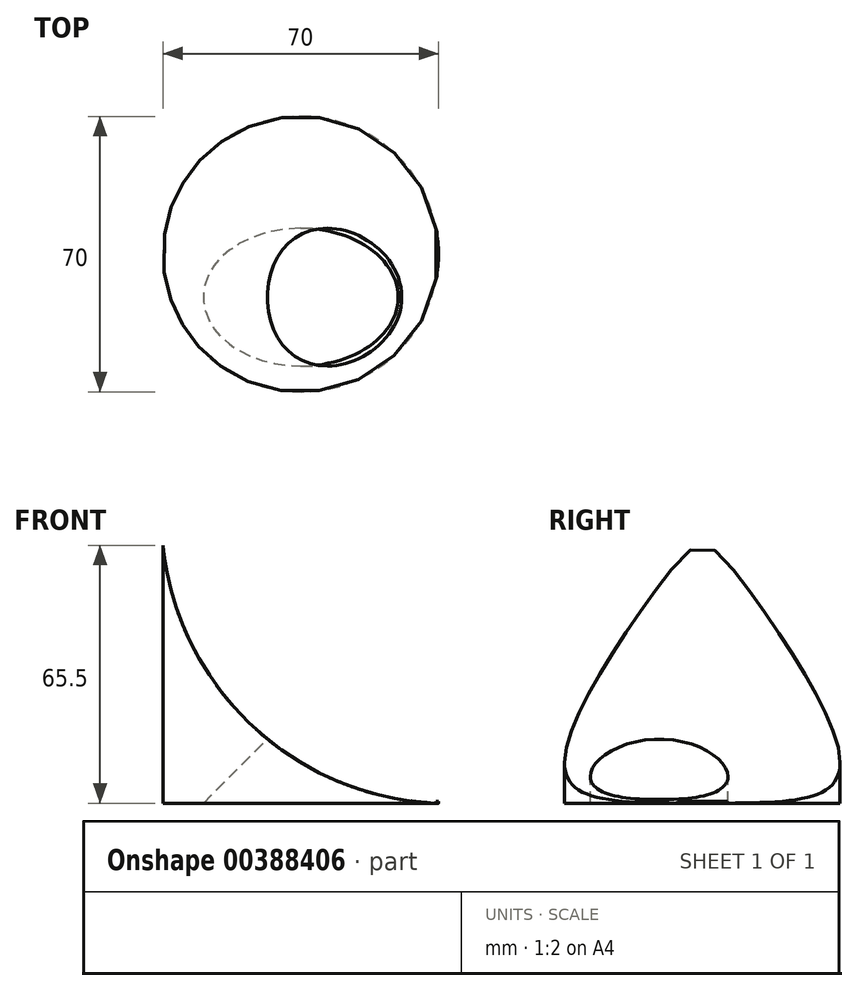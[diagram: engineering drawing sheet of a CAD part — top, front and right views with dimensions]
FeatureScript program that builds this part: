
annotation { "Feature Type Name" : "Feature", "Feature Type Description" : "" }
export const myFeature = defineFeature(function(context is Context, id is Id, definition is map)
    precondition{}
    {
        {
            var Q0;
            Q0=qCreatedBy(makeId("Top.planeOp"),FACE);
            var sketch = newSketch(context, id + "F0", { "sketchPlane" : qUnion([Q0])});
            skCircle(sketch, "E0", {"center": v(0, 0) * mm, "radius": 35 * mm});
            skSolve(sketch);
        }
        {
            var Q0;
            Q0=makeQuery(id+"F0.imprint","IMPRINT",FACE,{"disambiguationData":[TD([[makeQuery(id+"F0.imprint","IMPRINT",EDGE,{"derivedFrom":sQuery(id+"F0.wireOp",EDGE,"E0")}),1.0]])]});
            extrude(context, id + "F1", {"entities" : qUnion([Q0]), "depth" : 65.5 * mm, "offsetDistance" : 25 * mm});
        }
        {
            var Q0;
            Q0=qCreatedBy(makeId("Front.planeOp"),FACE);
            var sketch = newSketch(context, id + "F2", { "sketchPlane" : qUnion([Q0])});
            skLineSegment(sketch, "E1", {"start": v(0, 0) * mm, "end": v(-35, 0) * mm});
            skLineSegment(sketch, "E2", {"start": v(-35, 65.5) * mm, "end": v(34.42, 65.5) * mm});
            skLineSegment(sketch, "E3", {"start": v(34.42, 65.5) * mm, "end": v(34.42, 0) * mm});
            skArc(sketch, "E4", {"start": v(-35, 65.5) * mm, "mid": v(-12.5, 19.8) * mm, "end": v(34.42, 0) * mm});
            skSolve(sketch);
        }
        {
            var Q0;
            Q0 = qSketchRegion(id + "F2", true);
            extrude(context, id + "F3", {"entities" : qUnion([Q0]), "operationType" : NewBodyOperationType.ADD, "depth" : 35 * mm, "offsetDistance" : 25 * mm});
        }
        {
            var Q0;
            Q0=makeQuery(id+"F3.opExtrude","CAP_FACE",FACE,{"disambiguationData":[OSD([sQuery(id+"F2.wireOp",EDGE,"E2"),sQuery(id+"F2.wireOp",EDGE,"E3"),sQuery(id+"F2.wireOp",EDGE,"E4")])],"isStart":false});
            extrude(context, id + "F4", {"entities" : qUnion([Q0]), "operationType" : NewBodyOperationType.REMOVE, "oppositeDirection" : true, "depth" : 83.4 * mm, "offsetDistance" : 25 * mm});
        }
        {
            var Q0;
            Q0=makeQuery(id+"F3.boolean.opBoolean","MERGE",FACE,{"derivedFrom":[makeQuery(id+"F1.opExtrude","CAP_FACE",FACE,{"disambiguationData":[OSD([sQuery(id+"F0.wireOp",EDGE,"E0")])],"isStart":false}),makeQuery(id+"F3.opExtrude","SWEPT_FACE",FACE,{"disambiguationData":[OSD([sQuery(id+"F2.wireOp",EDGE,"E2")])]})]});
            extrude(context, id + "F5", {"entities" : qUnion([Q0]), "operationType" : NewBodyOperationType.REMOVE, "oppositeDirection" : true, "depth" : 65 * mm, "offsetDistance" : 25 * mm});
        }
        {
            var Q0;
            Q0=qCreatedBy(makeId("Front.planeOp"),FACE);
            var sketch = newSketch(context, id + "F6", { "sketchPlane" : qUnion([Q0])});
            skLineSegment(sketch, "E5", {"start": v(0, 0) * mm, "end": v(0, 32.75) * mm});
            skLineSegment(sketch, "E6.bottom", {"start": v(3.18, 32.75) * mm, "end": v(-3.18, 32.75) * mm});
            skLineSegment(sketch, "E6.top", {"start": v(3.18, 34.76) * mm, "end": v(-3.18, 34.76) * mm});
            skLineSegment(sketch, "E6.left", {"start": v(3.18, 32.75) * mm, "end": v(3.18, 34.76) * mm});
            skLineSegment(sketch, "E6.right", {"start": v(-3.18, 32.75) * mm, "end": v(-3.18, 34.76) * mm});
            skPoint(sketch, "E6.middle", {"position": v(0, 33.76) * mm});
            skSolve(sketch);
        }
        {
            var Q0;
            Q0=makeQuery(id+"F6.imprint","IMPRINT",FACE,{"disambiguationData":[TD([[makeQuery(id+"F6.imprint","IMPRINT",EDGE,{"derivedFrom":sQuery(id+"F6.wireOp",EDGE,"E6.top")}),1.0]])]});
            extrude(context, id + "F7", {"entities" : qUnion([Q0]), "depth" : 25 * mm, "offsetDistance" : 25 * mm});
        }
        {
            var Q0;
            Q0=makeQuery(id+"F7.opExtrude","CAP_FACE",FACE,{"disambiguationData":[OSD([sQuery(id+"F6.wireOp",EDGE,"E6.bottom"),sQuery(id+"F6.wireOp",EDGE,"E6.top"),sQuery(id+"F6.wireOp",EDGE,"E6.left"),sQuery(id+"F6.wireOp",EDGE,"E6.right")])],"isStart":true});
            extrude(context, id + "F8", {"entities" : qUnion([Q0]), "operationType" : NewBodyOperationType.ADD, "depth" : 25 * mm, "offsetDistance" : 25 * mm});
        }
        {
            var Q0;
            {var subQ0=sQuery(id+"F6.wireOp",EDGE,"E6.left");var subQ1=sQuery(id+"F6.wireOp",EDGE,"E6.top");Q0=makeQuery(id+"F8.boolean.opBoolean","MERGE",EDGE,{"derivedFrom":[makeQuery(id+"F7.opExtrude","SWEPT_EDGE",EDGE,{"disambiguationData":[OSD([subQ1,subQ0])]}),makeQuery(id+"F8.opExtrude","SWEPT_EDGE",EDGE,{"disambiguationData":[OSD([subQ1,subQ0])]})]});}
            cPlane(context, id + "F9", {"entities" : qUnion([Q0]), "cplaneType" : CPlaneType.LINE_ANGLE, "offset" : 25 * mm, "angle" : 45 * degree, "width" : 150 * mm, "height" : 150 * mm});
        }
        {
            var Q0;
            Q0=qCreatedBy(id+"F9.planeOp",FACE);
            var sketch = newSketch(context, id + "F10", { "sketchPlane" : qUnion([Q0])});
            skCircle(sketch, "E7", {"center": v(-10.94, 0) * mm, "radius": 17.5 * mm});
            skSolve(sketch);
        }
        {
            var Q0;
            Q0=makeQuery(id+"F7.opExtrude","CAP_FACE",FACE,{"disambiguationData":[OSD([sQuery(id+"F6.wireOp",EDGE,"E6.bottom"),sQuery(id+"F6.wireOp",EDGE,"E6.top"),sQuery(id+"F6.wireOp",EDGE,"E6.left"),sQuery(id+"F6.wireOp",EDGE,"E6.right")])],"isStart":false});
            extrude(context, id + "F11", {"entities" : qUnion([Q0]), "operationType" : NewBodyOperationType.REMOVE, "oppositeDirection" : true, "depth" : 100 * mm, "offsetDistance" : 25 * mm});
        }
        {
            var Q0;
            Q0=makeQuery(id+"F10.imprint","IMPRINT",FACE,{"disambiguationData":[TD([[makeQuery(id+"F10.imprint","IMPRINT",EDGE,{"derivedFrom":sQuery(id+"F10.wireOp",EDGE,"E7")}),1.0]])]});
            extrude(context, id + "F12", {"entities" : qUnion([Q0]), "operationType" : NewBodyOperationType.REMOVE, "oppositeDirection" : true, "depth" : 49.7 * mm, "offsetDistance" : 25 * mm});
        }
    });
